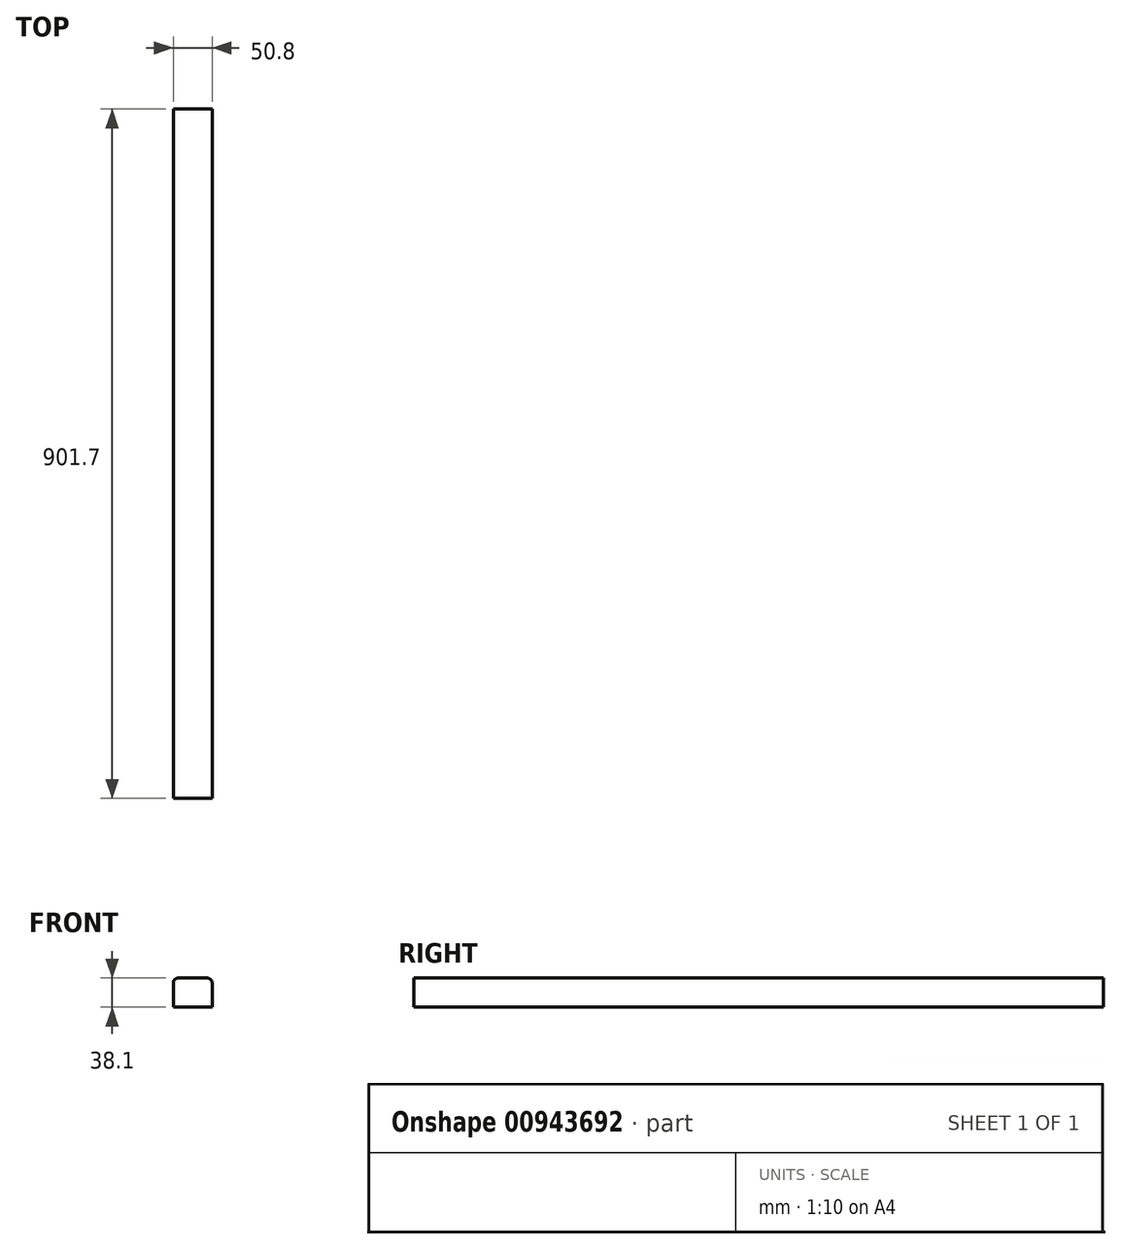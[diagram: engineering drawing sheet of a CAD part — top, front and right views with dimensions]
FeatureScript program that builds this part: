
annotation { "Feature Type Name" : "Feature", "Feature Type Description" : "" }
export const myFeature = defineFeature(function(context is Context, id is Id, definition is map)
    precondition{}
    {
        {
            var Q0;
            Q0=qCreatedBy(makeId("Front.planeOp"),FACE);
            var sketch = newSketch(context, id + "F0", { "sketchPlane" : qUnion([Q0])});
            skLineSegment(sketch, "E0.bottom", {"start": v(-25.4, -19.05) * mm, "end": v(25.4, -19.05) * mm});
            skLineSegment(sketch, "E0.top", {"start": v(-19.05, 19.05) * mm, "end": v(19.05, 19.05) * mm});
            skLineSegment(sketch, "E0.left", {"start": v(-25.4, -19.05) * mm, "end": v(-25.4, 12.7) * mm});
            skLineSegment(sketch, "E0.right", {"start": v(25.4, -19.05) * mm, "end": v(25.4, 12.7) * mm});
            skPoint(sketch, "E0.middle", {"position": v(0, 0) * mm});
            skPoint(sketch, "E1.visualSharp", {"position": v(-25.4, 19.05) * mm});
            skArc(sketch, "E1.filletArc", {"start": v(-19.05, 19.05) * mm, "mid": v(-23.54, 17.2) * mm, "end": v(-25.4, 12.7) * mm});
            skPoint(sketch, "E2.visualSharp", {"position": v(25.4, 19.05) * mm});
            skArc(sketch, "E2.filletArc", {"start": v(25.4, 12.7) * mm, "mid": v(23.54, 17.2) * mm, "end": v(19.05, 19.05) * mm});
            skSolve(sketch);
        }
        {
            var Q0;
            Q0=makeQuery(id+"F0.imprint","IMPRINT",FACE,{"disambiguationData":[TD([[makeQuery(id+"F0.imprint","IMPRINT",EDGE,{"derivedFrom":sQuery(id+"F0.wireOp",EDGE,"E0.bottom")}),1.0]])]});
            extrude(context, id + "F1", {"entities" : qUnion([Q0]), "depth" : 901.7 * mm, "offsetDistance" : 25.4 * mm});
        }
    });
